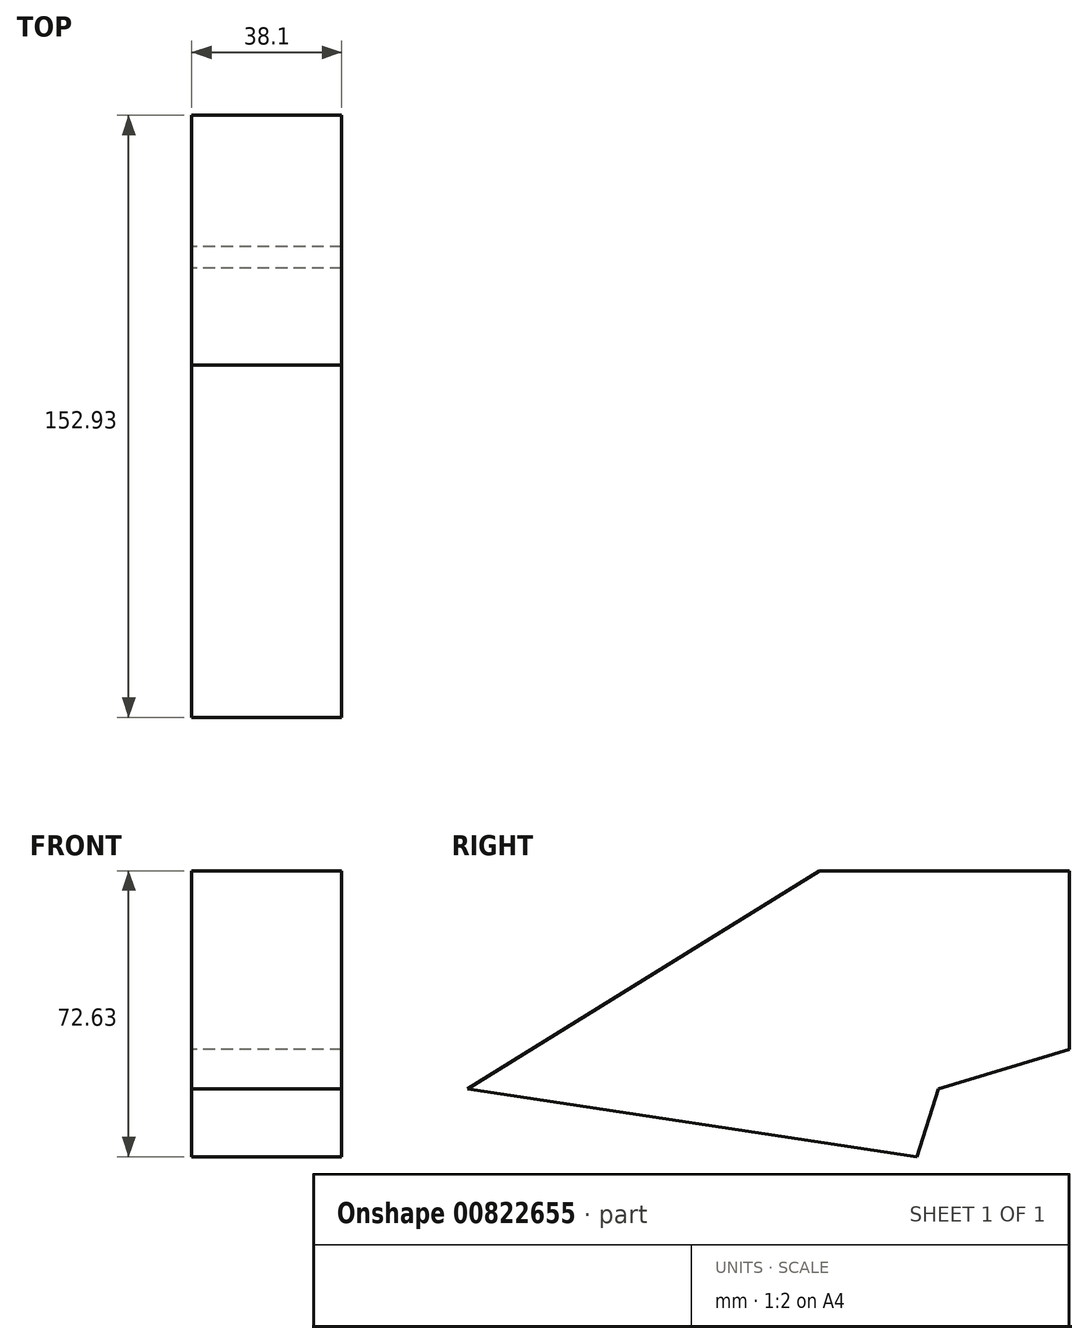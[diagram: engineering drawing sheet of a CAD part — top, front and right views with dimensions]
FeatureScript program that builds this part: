
annotation { "Feature Type Name" : "Feature", "Feature Type Description" : "" }
export const myFeature = defineFeature(function(context is Context, id is Id, definition is map)
    precondition{}
    {
        {
            var Q0;
            Q0=qCreatedBy(makeId("Right.planeOp"),FACE);
            var sketch = newSketch(context, id + "F0", { "sketchPlane" : qUnion([Q0])});
            skLineSegment(sketch, "E0", {"start": v(-53.25, 31.57) * mm, "end": v(36.18, 87.02) * mm});
            skLineSegment(sketch, "E1", {"start": v(36.18, 87.02) * mm, "end": v(99.68, 87.02) * mm});
            skLineSegment(sketch, "E2", {"start": v(99.68, 87.02) * mm, "end": v(99.68, 41.65) * mm});
            skLineSegment(sketch, "E3", {"start": v(99.68, 41.65) * mm, "end": v(66.39, 31.57) * mm});
            skLineSegment(sketch, "E4", {"start": v(66.39, 31.57) * mm, "end": v(60.86, 14.39) * mm});
            skLineSegment(sketch, "E5", {"start": v(-53.25, 31.57) * mm, "end": v(60.86, 14.39) * mm});
            skSolve(sketch);
        }
        {
            var Q0;
            Q0=makeQuery(id+"F0.imprint","IMPRINT",FACE,{"disambiguationData":[TD([[makeQuery(id+"F0.imprint","IMPRINT",EDGE,{"derivedFrom":sQuery(id+"F0.wireOp",EDGE,"E0")}),-1.0]])]});
            extrude(context, id + "F1", {"entities" : qUnion([Q0]), "endBound" : BoundingType.SYMMETRIC, "depth" : 38.1 * mm, "offsetDistance" : 25.4 * mm});
        }
        {
            var Q0;
            Q0 = qSketchRegion(id + "F0", true);
            extrude(context, id + "F2", {"entities" : qUnion([Q0]), "endBound" : BoundingType.SYMMETRIC, "depth" : 38.1 * mm, "offsetDistance" : 25.4 * mm});
        }
    });
